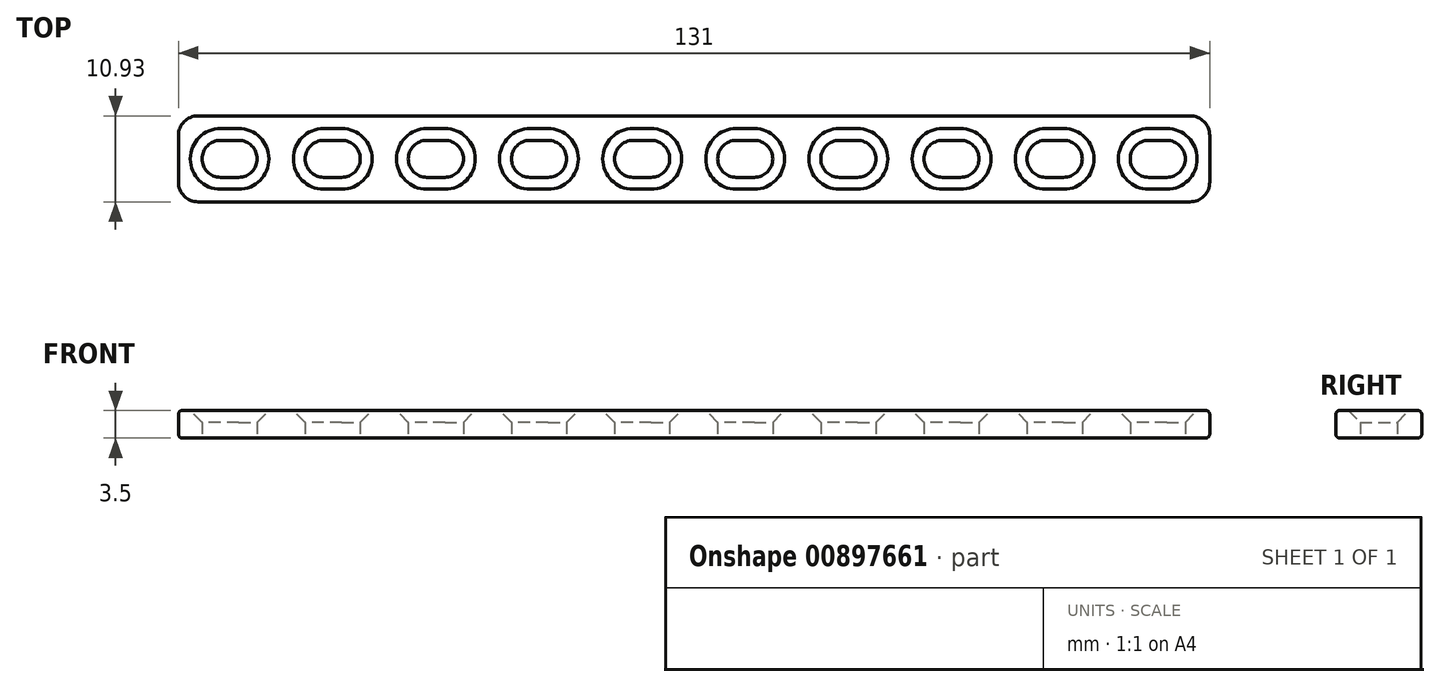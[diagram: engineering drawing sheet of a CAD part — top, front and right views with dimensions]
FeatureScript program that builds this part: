
annotation { "Feature Type Name" : "Feature", "Feature Type Description" : "" }
export const myFeature = defineFeature(function(context is Context, id is Id, definition is map)
    precondition{}
    {
        {
            var Q0;
            Q0=qCreatedBy(makeId("Top.planeOp"),FACE);
            var sketch = newSketch(context, id + "F0", { "sketchPlane" : qUnion([Q0])});
            skLineSegment(sketch, "E0", {"start": v(-67.55, -27.62) * mm, "end": v(58.45, -27.62) * mm});
            skLineSegment(sketch, "E1", {"start": v(-70.05, -25.12) * mm, "end": v(-70.05, -19.2) * mm});
            skLineSegment(sketch, "E2", {"start": v(-67.55, -16.7) * mm, "end": v(58.45, -16.7) * mm});
            skLineSegment(sketch, "E3", {"start": v(60.95, -19.2) * mm, "end": v(60.95, -25.12) * mm});
            skLineSegment(sketch, "E4", {"start": v(-70.05, -22.16) * mm, "end": v(60.95, -22.16) * mm, "construction": true});
            skArc(sketch, "E5", {"start": v(-64.7, -19.8) * mm, "mid": v(-67.05, -22.16) * mm, "end": v(-64.7, -24.5) * mm});
            skArc(sketch, "E6.1.0.0", {"start": v(-62.4, -24.5) * mm, "mid": v(-60.05, -22.16) * mm, "end": v(-62.4, -19.8) * mm});
            skLineSegment(sketch, "E6.direction1", {"start": v(-64.7, -22.16) * mm, "end": v(-62.4, -22.16) * mm, "construction": true});
            skLineSegment(sketch, "E7", {"start": v(-62.4, -19.8) * mm, "end": v(-64.7, -19.8) * mm});
            skLineSegment(sketch, "E8", {"start": v(-64.7, -24.5) * mm, "end": v(-62.4, -24.5) * mm});
            skArc(sketch, "E9.1.0.0", {"start": v(-51.6, -19.8) * mm, "mid": v(-53.95, -22.16) * mm, "end": v(-51.6, -24.5) * mm});
            skArc(sketch, "E9.1.0.1", {"start": v(-49.3, -24.5) * mm, "mid": v(-46.95, -22.16) * mm, "end": v(-49.3, -19.8) * mm});
            skLineSegment(sketch, "E9.1.0.2", {"start": v(-49.3, -19.8) * mm, "end": v(-51.6, -19.8) * mm});
            skLineSegment(sketch, "E9.1.0.3", {"start": v(-51.6, -24.5) * mm, "end": v(-49.3, -24.5) * mm});
            skArc(sketch, "E9.2.0.0", {"start": v(-38.5, -19.8) * mm, "mid": v(-40.85, -22.16) * mm, "end": v(-38.5, -24.5) * mm});
            skArc(sketch, "E9.2.0.1", {"start": v(-36.2, -24.5) * mm, "mid": v(-33.85, -22.16) * mm, "end": v(-36.2, -19.8) * mm});
            skLineSegment(sketch, "E9.2.0.2", {"start": v(-36.2, -19.8) * mm, "end": v(-38.5, -19.8) * mm});
            skLineSegment(sketch, "E9.2.0.3", {"start": v(-38.5, -24.5) * mm, "end": v(-36.2, -24.5) * mm});
            skLineSegment(sketch, "E9.direction1", {"start": v(-64.7, -24.5) * mm, "end": v(-51.6, -24.5) * mm, "construction": true});
            skArc(sketch, "E10.0.3.0", {"start": v(-25.4, -19.8) * mm, "mid": v(-27.75, -22.16) * mm, "end": v(-25.4, -24.5) * mm});
            skArc(sketch, "E10.4.3.0", {"start": v(-23.1, -24.5) * mm, "mid": v(-20.75, -22.16) * mm, "end": v(-23.1, -19.8) * mm});
            skLineSegment(sketch, "E10.8.3.0", {"start": v(-23.1, -19.8) * mm, "end": v(-25.4, -19.8) * mm});
            skLineSegment(sketch, "E10.11.3.0", {"start": v(-25.4, -24.5) * mm, "end": v(-23.1, -24.5) * mm});
            skArc(sketch, "E10.0.4.0", {"start": v(-12.3, -19.8) * mm, "mid": v(-14.65, -22.16) * mm, "end": v(-12.3, -24.5) * mm});
            skArc(sketch, "E10.4.4.0", {"start": v(-10, -24.5) * mm, "mid": v(-7.65, -22.16) * mm, "end": v(-10, -19.8) * mm});
            skLineSegment(sketch, "E10.8.4.0", {"start": v(-10, -19.8) * mm, "end": v(-12.3, -19.8) * mm});
            skLineSegment(sketch, "E10.11.4.0", {"start": v(-12.3, -24.5) * mm, "end": v(-10, -24.5) * mm});
            skArc(sketch, "E10.0.5.0", {"start": v(0.8, -19.8) * mm, "mid": v(-1.55, -22.16) * mm, "end": v(0.8, -24.5) * mm});
            skArc(sketch, "E10.4.5.0", {"start": v(3.1, -24.5) * mm, "mid": v(5.45, -22.16) * mm, "end": v(3.1, -19.8) * mm});
            skLineSegment(sketch, "E10.8.5.0", {"start": v(3.1, -19.8) * mm, "end": v(0.8, -19.8) * mm});
            skLineSegment(sketch, "E10.11.5.0", {"start": v(0.8, -24.5) * mm, "end": v(3.1, -24.5) * mm});
            skArc(sketch, "E10.0.6.0", {"start": v(13.9, -19.8) * mm, "mid": v(11.55, -22.16) * mm, "end": v(13.9, -24.5) * mm});
            skArc(sketch, "E10.4.6.0", {"start": v(16.2, -24.5) * mm, "mid": v(18.55, -22.16) * mm, "end": v(16.2, -19.8) * mm});
            skLineSegment(sketch, "E10.8.6.0", {"start": v(16.2, -19.8) * mm, "end": v(13.9, -19.8) * mm});
            skLineSegment(sketch, "E10.11.6.0", {"start": v(13.9, -24.5) * mm, "end": v(16.2, -24.5) * mm});
            skArc(sketch, "E10.0.7.0", {"start": v(27, -19.8) * mm, "mid": v(24.65, -22.16) * mm, "end": v(27, -24.5) * mm});
            skArc(sketch, "E10.4.7.0", {"start": v(29.3, -24.5) * mm, "mid": v(31.65, -22.16) * mm, "end": v(29.3, -19.8) * mm});
            skLineSegment(sketch, "E10.8.7.0", {"start": v(29.3, -19.8) * mm, "end": v(27, -19.8) * mm});
            skLineSegment(sketch, "E10.11.7.0", {"start": v(27, -24.5) * mm, "end": v(29.3, -24.5) * mm});
            skArc(sketch, "E10.0.8.0", {"start": v(40.1, -19.8) * mm, "mid": v(37.75, -22.16) * mm, "end": v(40.1, -24.5) * mm});
            skArc(sketch, "E10.4.8.0", {"start": v(42.4, -24.5) * mm, "mid": v(44.75, -22.16) * mm, "end": v(42.4, -19.8) * mm});
            skLineSegment(sketch, "E10.8.8.0", {"start": v(42.4, -19.8) * mm, "end": v(40.1, -19.8) * mm});
            skLineSegment(sketch, "E10.11.8.0", {"start": v(40.1, -24.5) * mm, "end": v(42.4, -24.5) * mm});
            skArc(sketch, "E10.0.9.0", {"start": v(53.2, -19.8) * mm, "mid": v(50.85, -22.16) * mm, "end": v(53.2, -24.5) * mm});
            skArc(sketch, "E10.4.9.0", {"start": v(55.5, -24.5) * mm, "mid": v(57.85, -22.16) * mm, "end": v(55.5, -19.8) * mm});
            skLineSegment(sketch, "E10.8.9.0", {"start": v(55.5, -19.8) * mm, "end": v(53.2, -19.8) * mm});
            skLineSegment(sketch, "E10.11.9.0", {"start": v(53.2, -24.5) * mm, "end": v(55.5, -24.5) * mm});
            skPoint(sketch, "E11", {"position": v(-87.31, -55.63) * mm});
            skPoint(sketch, "E12.visualSharp", {"position": v(60.95, -27.62) * mm});
            skArc(sketch, "E12.filletArc", {"start": v(58.45, -27.62) * mm, "mid": v(60.21, -26.88) * mm, "end": v(60.95, -25.12) * mm});
            skPoint(sketch, "E13.visualSharp", {"position": v(60.95, -16.7) * mm});
            skArc(sketch, "E13.filletArc", {"start": v(60.95, -19.2) * mm, "mid": v(60.21, -17.43) * mm, "end": v(58.45, -16.7) * mm});
            skPoint(sketch, "E14.visualSharp", {"position": v(-70.05, -16.7) * mm});
            skArc(sketch, "E14.filletArc", {"start": v(-67.55, -16.7) * mm, "mid": v(-69.32, -17.43) * mm, "end": v(-70.05, -19.2) * mm});
            skPoint(sketch, "E15.visualSharp", {"position": v(-70.05, -27.62) * mm});
            skArc(sketch, "E15.filletArc", {"start": v(-70.05, -25.12) * mm, "mid": v(-69.32, -26.88) * mm, "end": v(-67.55, -27.62) * mm});
            skSolve(sketch);
        }
        {
            var Q0;
            Q0=makeQuery(id+"F0.imprint","IMPRINT",FACE,{"disambiguationData":[TD([[makeQuery(id+"F0.imprint","IMPRINT",EDGE,{"derivedFrom":sQuery(id+"F0.wireOp",EDGE,"E0")}),1.0]])]});
            extrude(context, id + "F1", {"entities" : qUnion([Q0]), "depth" : 3.5 * mm, "offsetDistance" : 25 * mm});
        }
        {
            var Q0;
            Q0=makeQuery(id+"F1.opExtrude","CAP_EDGE",EDGE,{"disambiguationData":[OSD([sQuery(id+"F0.wireOp",EDGE,"E6.1.0.0")])],"isStart":false});
            var Q1;
            Q1=makeQuery(id+"F1.opExtrude","CAP_EDGE",EDGE,{"disambiguationData":[OSD([sQuery(id+"F0.wireOp",EDGE,"E9.1.0.1")])],"isStart":false});
            var Q2;
            Q2=makeQuery(id+"F1.opExtrude","CAP_EDGE",EDGE,{"disambiguationData":[OSD([sQuery(id+"F0.wireOp",EDGE,"E9.2.0.1")])],"isStart":false});
            var Q3;
            Q3=makeQuery(id+"F1.opExtrude","CAP_EDGE",EDGE,{"disambiguationData":[OSD([sQuery(id+"F0.wireOp",EDGE,"E10.4.3.0")])],"isStart":false});
            var Q4;
            Q4=makeQuery(id+"F1.opExtrude","CAP_EDGE",EDGE,{"disambiguationData":[OSD([sQuery(id+"F0.wireOp",EDGE,"E10.4.4.0")])],"isStart":false});
            var Q5;
            Q5=makeQuery(id+"F1.opExtrude","CAP_EDGE",EDGE,{"disambiguationData":[OSD([sQuery(id+"F0.wireOp",EDGE,"E10.4.5.0")])],"isStart":false});
            var Q6;
            Q6=makeQuery(id+"F1.opExtrude","CAP_EDGE",EDGE,{"disambiguationData":[OSD([sQuery(id+"F0.wireOp",EDGE,"E10.4.6.0")])],"isStart":false});
            var Q7;
            Q7=makeQuery(id+"F1.opExtrude","CAP_EDGE",EDGE,{"disambiguationData":[OSD([sQuery(id+"F0.wireOp",EDGE,"E10.4.7.0")])],"isStart":false});
            var Q8;
            Q8=makeQuery(id+"F1.opExtrude","CAP_EDGE",EDGE,{"disambiguationData":[OSD([sQuery(id+"F0.wireOp",EDGE,"E10.4.8.0")])],"isStart":false});
            var Q9;
            Q9=makeQuery(id+"F1.opExtrude","CAP_EDGE",EDGE,{"disambiguationData":[OSD([sQuery(id+"F0.wireOp",EDGE,"E10.4.9.0")])],"isStart":false});
            chamfer(context, id + "F2", {"entities" : qUnion([Q0, Q1, Q2, Q3, Q4, Q5, Q6, Q7, Q8, Q9]), "width" : 1.5 * mm, "tangentPropagation" : true});
        }
        {
            var Q0;
            Q0=makeQuery(id+"F1.opExtrude","CAP_EDGE",EDGE,{"disambiguationData":[OSD([sQuery(id+"F0.wireOp",EDGE,"E0")])],"isStart":false});
            var Q1;
            Q1=makeQuery(id+"F1.opExtrude","CAP_EDGE",EDGE,{"disambiguationData":[OSD([sQuery(id+"F0.wireOp",EDGE,"E0")])],"isStart":true});
            fillet(context, id + "F3", {"entities" : qUnion([Q0, Q1]), "radius" : .5 * mm, "tangentPropagation" : true, "allowEdgeOverflow" : false});
        }
    });
